# Revit family: Royal- 152-ESS-TMO-SBX_Series
name_source: partatom
category: Plumbing Fixtures
revit_build: Autodesk Revit 2016 (Build: 20150714_1515(x64)
units: mm (PartAtom-declared; Revit-internal decimal feet)

## family parameters
Always vertical = No
Cut with Voids When Loaded = No
OmniClass Number = 23.65.00.00
OmniClass Title = Supply and Distribution of Liquids and Gases
Part Type = Normal
Room Calculation Point = No
Round Connector Dimension = Use Diameter
Shared = Yes
Work Plane-Based = Yes

## types (3) — shared parameters
ADA Compliant = Yes
Assembly Code = D2020300
Buy American Act Compliant = Yes
CW Connection = Yes
CWFU = 10
Connection Size = 1"
Default Elevation = 0"
Finish = Metal-Sloan-Semi-red Brass Chrome
Flush Choice = Single Flush
HW Connection = No
High-Efficiency = Yes
IAPMO Certification = UPC
Inlet Spud Size = 1'' IPS
Manufacturer = SLOAN
Material = Metal-Sloan-Semi-red Brass Chrome
Mounting = Concealed
Operation = Sensor-Activated
Price = Prices may vary. Please consult Sloan Rep for most up-to-date price list.
Product URL = https://www.sloan.com
SWB Size = 13 1/2"
Spud Location = Rear Spud
URL = www.sloanvalve.com
Vent Connection = No
WFU = 10
Warranty = 3 Year (Limited)
Waste Connection = No
zero-valued in all types: HWFU

## per-type parameters (varying)
| type | Description | Flush Volume(s)/Flow Rate(s) | Wall Thikness + 2 3/4" |
| Royal 152-1.6 ESS TMO SBX | 1.6 gpf, Rough Brass Finish, Single Flush, 2-10.75 L Dimension, True Mechanical Override, Hardwired, Sensor-Operated, Small Wall Box, Royal® Concealed Sensor Hardwired Water Closet Flushometer. | 1.6 gpf (6.0 Lpf) | 3" |
| Royal 152-1.28 ESS TMO SBX | 1.28 gpf, Rough Brass Finish, Single Flush, 2-10.75 L Dimension, True Mechanical Override, Hardwired, Sensor-Operated, Small Wall Box, Royal® Concealed Sensor Hardwired Water Closet Flushometer. | 1.28 gpf (4.8 Lpf) | 5" |
| Royal 152-3.5 ESS TMO SBX | 3.5 gpf, Rough Brass Finish, Single Flush, 2-10.75 L Dimension, True Mechanical Override, Hardwired, Sensor-Operated, Small Wall Box, Royal® Concealed Sensor Hardwired Water Closet Flushometer. | 3.5 gpf (13.2 Lpf) | 3" |

note: column(s) folded — value = type name in every type: Model

## geometry (parser evidence)
native form markers: Sweep x2
no freeform markers — native parametric forms only
